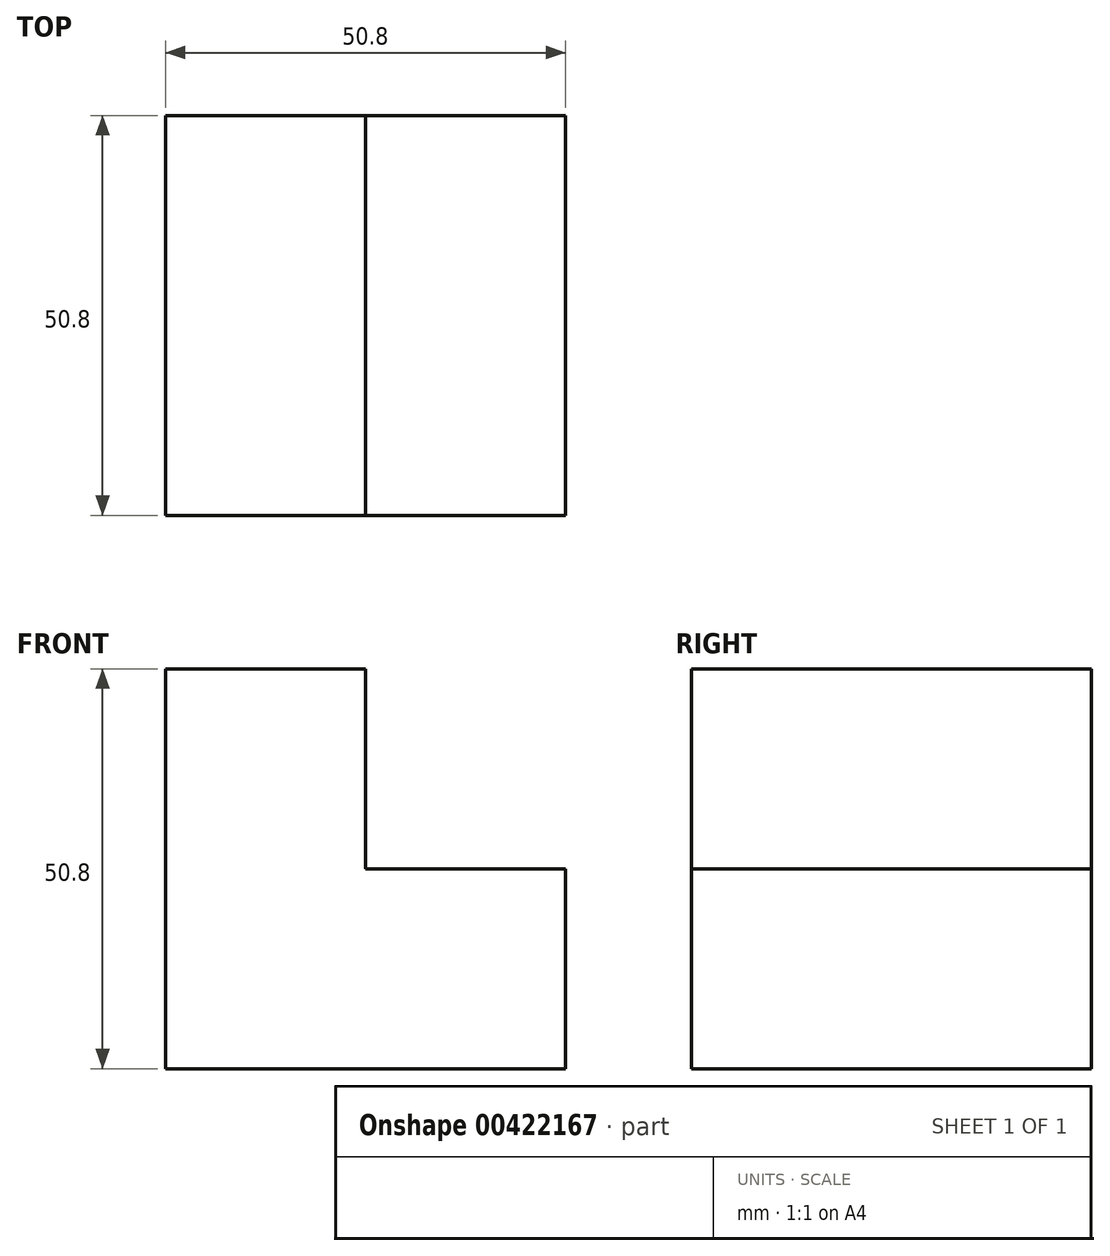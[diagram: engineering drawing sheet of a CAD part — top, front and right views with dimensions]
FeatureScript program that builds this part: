
annotation { "Feature Type Name" : "Feature", "Feature Type Description" : "" }
export const myFeature = defineFeature(function(context is Context, id is Id, definition is map)
    precondition{}
    {
        {
            var Q0;
            Q0=qCreatedBy(makeId("Front.planeOp"),FACE);
            var sketch = newSketch(context, id + "F0", { "sketchPlane" : qUnion([Q0])});
            skLineSegment(sketch, "E0", {"start": v(-37.69, 57.8) * mm, "end": v(-37.69, 7) * mm});
            skLineSegment(sketch, "E1", {"start": v(-37.69, 7) * mm, "end": v(13.11, 7) * mm});
            skLineSegment(sketch, "E2", {"start": v(13.11, 7) * mm, "end": v(13.11, 32.4) * mm});
            skLineSegment(sketch, "E3", {"start": v(13.11, 32.4) * mm, "end": v(-12.29, 32.4) * mm});
            skLineSegment(sketch, "E4", {"start": v(-12.29, 32.4) * mm, "end": v(-12.29, 57.8) * mm});
            skLineSegment(sketch, "E5", {"start": v(-12.29, 57.8) * mm, "end": v(-37.69, 57.8) * mm});
            skSolve(sketch);
        }
        {
            var Q0;
            Q0 = qSketchRegion(id + "F0", true);
            extrude(context, id + "F1", {"entities" : qUnion([Q0]), "depth" : 50.8 * mm});
        }
    });
